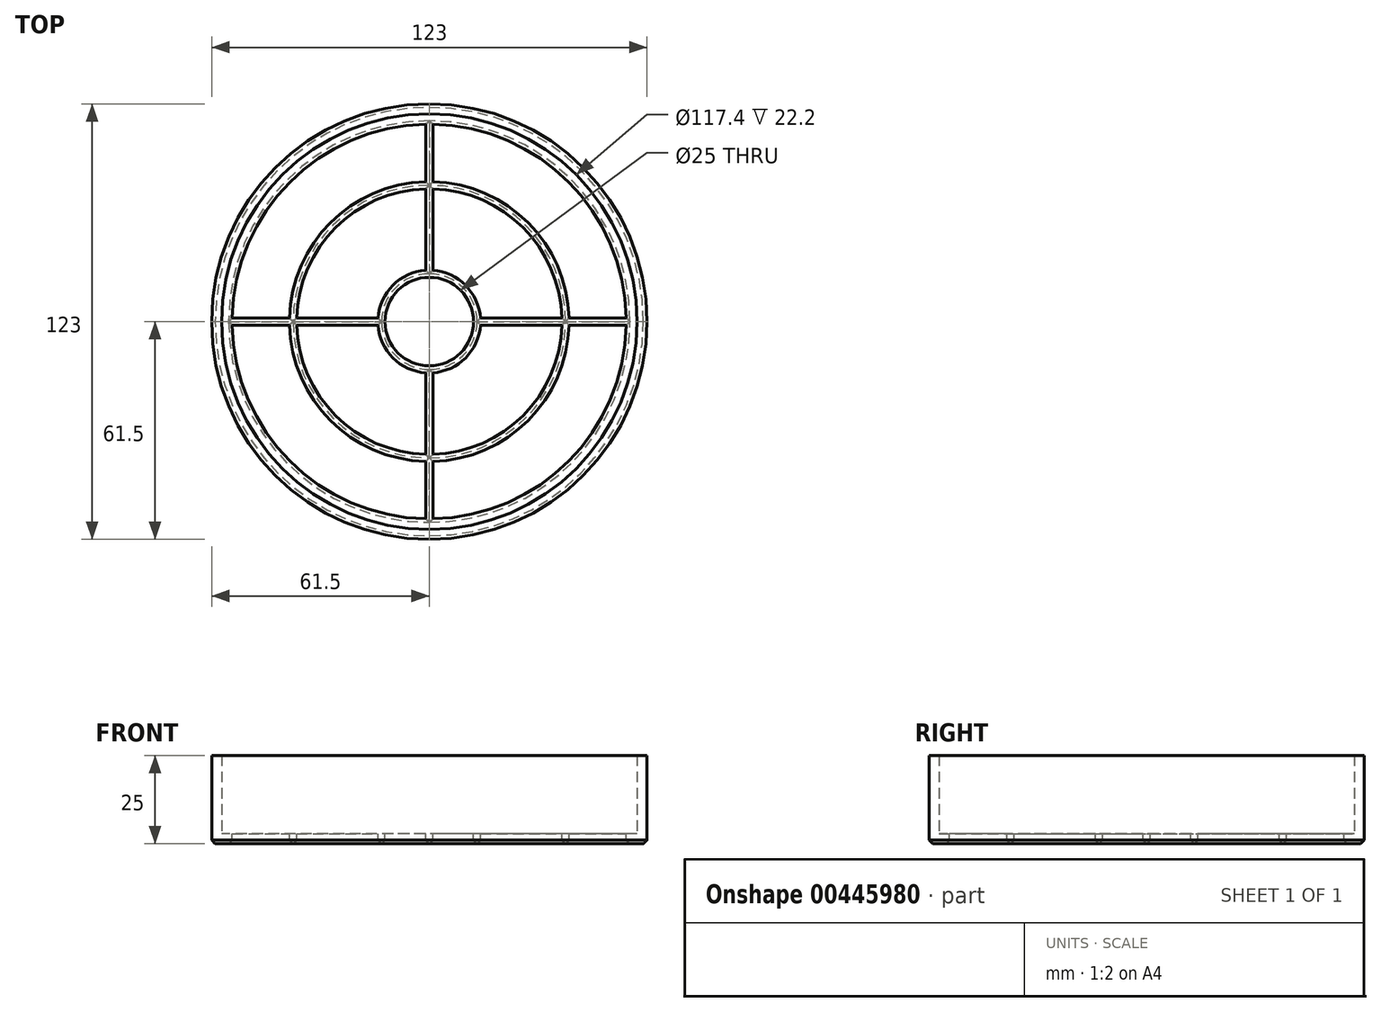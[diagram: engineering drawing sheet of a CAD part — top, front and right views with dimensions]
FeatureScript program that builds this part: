
annotation { "Feature Type Name" : "Feature", "Feature Type Description" : "" }
export const myFeature = defineFeature(function(context is Context, id is Id, definition is map)
    precondition{}
    {
        {
            var Q0;
            Q0=qCreatedBy(makeId("Top.planeOp"),FACE);
            var sketch = newSketch(context, id + "F0", { "sketchPlane" : qUnion([Q0])});
            skCircle(sketch, "E0", {"center": v(0, 0) * mm, "radius": 61.5 * mm});
            skSolve(sketch);
        }
        {
            var Q0;
            Q0=makeQuery(id+"F0.imprint","IMPRINT",FACE,{"disambiguationData":[TD([[makeQuery(id+"F0.imprint","IMPRINT",EDGE,{"derivedFrom":sQuery(id+"F0.wireOp",EDGE,"E0")}),1.0]])]});
            extrude(context, id + "F1", {"entities" : qUnion([Q0]), "depth" : 25 * mm});
        }
        {
            var Q0;
            Q0=makeQuery(id+"F1.opExtrude","CAP_FACE",FACE,{"disambiguationData":[OSD([sQuery(id+"F0.wireOp",EDGE,"E0")])],"isStart":false});
            shell(context, id + "F2", {"entities" : qUnion([Q0]), "thickness" : 2.8 * mm});
        }
        {
            var Q0;
            {var subQ0=sQuery(id+"F0.wireOp",EDGE,"E0");Q0=makeQuery(id+"F2.opShell","OFFSET_FACE",FACE,{"disambiguationData":[OSD([subQ0]),TDD([makeQuery(id+"F1.opExtrude","CAP_FACE",FACE,{"disambiguationData":[OSD([subQ0])],"isStart":true})])]});}
            var sketch = newSketch(context, id + "F3", { "sketchPlane" : qUnion([Q0])});
            skCircle(sketch, "E1", {"center": v(0, 0) * mm, "radius": 55.7 * mm});
            skCircle(sketch, "E2", {"center": v(0, 0) * mm, "radius": 39.5 * mm});
            skCircle(sketch, "E3", {"center": v(0, 0) * mm, "radius": 37.5 * mm});
            skCircle(sketch, "E4", {"center": v(0, 0) * mm, "radius": 14.5 * mm});
            skCircle(sketch, "E5", {"center": v(0, 0) * mm, "radius": 12.5 * mm});
            skLineSegment(sketch, "E6", {"start": v(-1, 55.7) * mm, "end": v(-1, -55.7) * mm});
            skLineSegment(sketch, "E7", {"start": v(1, 55.7) * mm, "end": v(1, -55.7) * mm});
            skPoint(sketch, "E8.center", {"position": v(-1, 0) * mm});
            skLineSegment(sketch, "E8.anchor1", {"start": v(-1, 0) * mm, "end": v(-1, -55.7) * mm, "construction": true});
            skLineSegment(sketch, "E9", {"start": v(-55.7, 1) * mm, "end": v(55.7, 1) * mm});
            skLineSegment(sketch, "E10", {"start": v(55.7, -1) * mm, "end": v(-55.7, -1) * mm});
            skSolve(sketch);
        }
        {
            var Q0;
            {var subQ0=sQuery(id+"F3.wireOp",EDGE,"E6");var subQ1=sQuery(id+"F3.wireOp",EDGE,"E3");var subQ2=makeQuery(id+"F3.imprint","INTERSECT",VERTEX,{"disambiguationData":[OD(0.0)],"derivedFrom":[subQ1,subQ0]});Q0=makeQuery(id+"F3.imprint","IMPRINT",FACE,{"disambiguationData":[TD([[makeQuery(id+"F3.imprint","IMPRINT",EDGE,{"disambiguationData":[TD([[subQ2,-1.0]])],"derivedFrom":subQ1}),1.0]])]});}
            var Q1;
            {var subQ0=sQuery(id+"F3.wireOp",EDGE,"E6");var subQ1=sQuery(id+"F3.wireOp",EDGE,"E1");var subQ2=makeQuery(id+"F3.imprint","INTERSECT",VERTEX,{"disambiguationData":[OD(0.0)],"derivedFrom":[subQ1,subQ0]});Q1=makeQuery(id+"F3.imprint","IMPRINT",FACE,{"disambiguationData":[TD([[makeQuery(id+"F3.imprint","IMPRINT",EDGE,{"disambiguationData":[TD([[subQ2,-1.0]])],"derivedFrom":subQ1}),1.0]])]});}
            var Q2;
            {var subQ0=sQuery(id+"F3.wireOp",EDGE,"E7");var subQ1=sQuery(id+"F3.wireOp",EDGE,"E1");var subQ2=makeQuery(id+"F3.imprint","INTERSECT",VERTEX,{"disambiguationData":[OD(0.0)],"derivedFrom":[subQ1,subQ0]});Q2=makeQuery(id+"F3.imprint","IMPRINT",FACE,{"disambiguationData":[TD([[makeQuery(id+"F3.imprint","IMPRINT",EDGE,{"disambiguationData":[TD([[subQ2,1.0]])],"derivedFrom":subQ1}),1.0]])]});}
            var Q3;
            {var subQ0=sQuery(id+"F3.wireOp",EDGE,"E7");var subQ1=sQuery(id+"F3.wireOp",EDGE,"E3");var subQ2=makeQuery(id+"F3.imprint","INTERSECT",VERTEX,{"disambiguationData":[OD(0.0)],"derivedFrom":[subQ1,subQ0]});Q3=makeQuery(id+"F3.imprint","IMPRINT",FACE,{"disambiguationData":[TD([[makeQuery(id+"F3.imprint","IMPRINT",EDGE,{"disambiguationData":[TD([[subQ2,1.0]])],"derivedFrom":subQ1}),1.0]])]});}
            var Q4;
            {var subQ0=sQuery(id+"F3.wireOp",EDGE,"E7");var subQ1=sQuery(id+"F3.wireOp",EDGE,"E1");var subQ2=makeQuery(id+"F3.imprint","INTERSECT",VERTEX,{"disambiguationData":[OD(1.0)],"derivedFrom":[subQ1,subQ0]});Q4=makeQuery(id+"F3.imprint","IMPRINT",FACE,{"disambiguationData":[TD([[makeQuery(id+"F3.imprint","IMPRINT",EDGE,{"disambiguationData":[TD([[subQ2,-1.0]])],"derivedFrom":subQ1}),1.0]])]});}
            var Q5;
            {var subQ0=sQuery(id+"F3.wireOp",EDGE,"E7");var subQ1=sQuery(id+"F3.wireOp",EDGE,"E3");var subQ2=makeQuery(id+"F3.imprint","INTERSECT",VERTEX,{"disambiguationData":[OD(1.0)],"derivedFrom":[subQ1,subQ0]});Q5=makeQuery(id+"F3.imprint","IMPRINT",FACE,{"disambiguationData":[TD([[makeQuery(id+"F3.imprint","IMPRINT",EDGE,{"disambiguationData":[TD([[subQ2,-1.0]])],"derivedFrom":subQ1}),1.0]])]});}
            var Q6;
            {var subQ0=sQuery(id+"F3.wireOp",EDGE,"E10");var subQ1=sQuery(id+"F3.wireOp",EDGE,"E3");var subQ2=makeQuery(id+"F3.imprint","INTERSECT",VERTEX,{"disambiguationData":[OD(0.0)],"derivedFrom":[subQ1,subQ0]});Q6=makeQuery(id+"F3.imprint","IMPRINT",FACE,{"disambiguationData":[TD([[makeQuery(id+"F3.imprint","IMPRINT",EDGE,{"disambiguationData":[TD([[subQ2,-1.0]])],"derivedFrom":subQ1}),1.0]])]});}
            var Q7;
            {var subQ0=sQuery(id+"F3.wireOp",EDGE,"E6");var subQ1=sQuery(id+"F3.wireOp",EDGE,"E1");var subQ2=makeQuery(id+"F3.imprint","INTERSECT",VERTEX,{"disambiguationData":[OD(1.0)],"derivedFrom":[subQ1,subQ0]});Q7=makeQuery(id+"F3.imprint","IMPRINT",FACE,{"disambiguationData":[TD([[makeQuery(id+"F3.imprint","IMPRINT",EDGE,{"disambiguationData":[TD([[subQ2,1.0]])],"derivedFrom":subQ1}),1.0]])]});}
            var Q8;
            {var subQ0=sQuery(id+"F3.wireOp",EDGE,"E10");var subQ1=sQuery(id+"F3.wireOp",EDGE,"E5");var subQ2=makeQuery(id+"F3.imprint","INTERSECT",VERTEX,{"disambiguationData":[OD(0.0)],"derivedFrom":[subQ1,subQ0]});Q8=makeQuery(id+"F3.imprint","IMPRINT",FACE,{"disambiguationData":[TD([[makeQuery(id+"F3.imprint","IMPRINT",EDGE,{"disambiguationData":[TD([[subQ2,-1.0]])],"derivedFrom":subQ1}),1.0]])]});}
            var Q9;
            {var subQ0=sQuery(id+"F3.wireOp",EDGE,"E9");var subQ1=sQuery(id+"F3.wireOp",EDGE,"E5");var subQ2=makeQuery(id+"F3.imprint","INTERSECT",VERTEX,{"disambiguationData":[OD(1.0)],"derivedFrom":[subQ1,subQ0]});Q9=makeQuery(id+"F3.imprint","IMPRINT",FACE,{"disambiguationData":[TD([[makeQuery(id+"F3.imprint","IMPRINT",EDGE,{"disambiguationData":[TD([[subQ2,-1.0]])],"derivedFrom":subQ1}),1.0]])]});}
            var Q10;
            {var subQ0=sQuery(id+"F3.wireOp",EDGE,"E6");var subQ1=sQuery(id+"F3.wireOp",EDGE,"E5");var subQ2=makeQuery(id+"F3.imprint","INTERSECT",VERTEX,{"disambiguationData":[OD(0.0)],"derivedFrom":[subQ1,subQ0]});Q10=makeQuery(id+"F3.imprint","IMPRINT",FACE,{"disambiguationData":[TD([[makeQuery(id+"F3.imprint","IMPRINT",EDGE,{"disambiguationData":[TD([[subQ2,-1.0]])],"derivedFrom":subQ1}),1.0]])]});}
            var Q11;
            {var subQ0=sQuery(id+"F3.wireOp",EDGE,"E7");var subQ1=sQuery(id+"F3.wireOp",EDGE,"E5");var subQ2=makeQuery(id+"F3.imprint","INTERSECT",VERTEX,{"disambiguationData":[OD(0.0)],"derivedFrom":[subQ1,subQ0]});Q11=makeQuery(id+"F3.imprint","IMPRINT",FACE,{"disambiguationData":[TD([[makeQuery(id+"F3.imprint","IMPRINT",EDGE,{"disambiguationData":[TD([[subQ2,-1.0]])],"derivedFrom":subQ1}),1.0]])]});}
            var Q12;
            {var subQ0=sQuery(id+"F3.wireOp",EDGE,"E7");var subQ1=sQuery(id+"F3.wireOp",EDGE,"E5");var subQ2=makeQuery(id+"F3.imprint","INTERSECT",VERTEX,{"disambiguationData":[OD(0.0)],"derivedFrom":[subQ1,subQ0]});Q12=makeQuery(id+"F3.imprint","IMPRINT",FACE,{"disambiguationData":[TD([[makeQuery(id+"F3.imprint","IMPRINT",EDGE,{"disambiguationData":[TD([[subQ2,1.0]])],"derivedFrom":subQ1}),1.0]])]});}
            var Q13;
            {var subQ0=sQuery(id+"F3.wireOp",EDGE,"E9");var subQ1=sQuery(id+"F3.wireOp",EDGE,"E5");var subQ2=makeQuery(id+"F3.imprint","INTERSECT",VERTEX,{"disambiguationData":[OD(0.0)],"derivedFrom":[subQ1,subQ0]});Q13=makeQuery(id+"F3.imprint","IMPRINT",FACE,{"disambiguationData":[TD([[makeQuery(id+"F3.imprint","IMPRINT",EDGE,{"disambiguationData":[TD([[subQ2,1.0]])],"derivedFrom":subQ1}),1.0]])]});}
            var Q14;
            {var subQ0=sQuery(id+"F3.wireOp",EDGE,"E7");var subQ1=sQuery(id+"F3.wireOp",EDGE,"E5");var subQ2=makeQuery(id+"F3.imprint","INTERSECT",VERTEX,{"disambiguationData":[OD(1.0)],"derivedFrom":[subQ1,subQ0]});Q14=makeQuery(id+"F3.imprint","IMPRINT",FACE,{"disambiguationData":[TD([[makeQuery(id+"F3.imprint","IMPRINT",EDGE,{"disambiguationData":[TD([[subQ2,-1.0]])],"derivedFrom":subQ1}),1.0]])]});}
            var Q15;
            {var subQ0=sQuery(id+"F3.wireOp",EDGE,"E6");var subQ1=sQuery(id+"F3.wireOp",EDGE,"E5");var subQ2=makeQuery(id+"F3.imprint","INTERSECT",VERTEX,{"disambiguationData":[OD(1.0)],"derivedFrom":[subQ1,subQ0]});Q15=makeQuery(id+"F3.imprint","IMPRINT",FACE,{"disambiguationData":[TD([[makeQuery(id+"F3.imprint","IMPRINT",EDGE,{"disambiguationData":[TD([[subQ2,-1.0]])],"derivedFrom":subQ1}),1.0]])]});}
            var Q16;
            {var subQ0=sQuery(id+"F3.wireOp",EDGE,"E9");var subQ1=sQuery(id+"F3.wireOp",EDGE,"E6");var subQ2=makeQuery(id+"F3.imprint","INTERSECT",VERTEX,{"derivedFrom":[subQ1,subQ0]});Q16=makeQuery(id+"F3.imprint","IMPRINT",FACE,{"disambiguationData":[TD([[makeQuery(id+"F3.imprint","IMPRINT",EDGE,{"disambiguationData":[TD([[subQ2,-1.0]])],"derivedFrom":subQ1}),1.0]])]});}
            extrude(context, id + "F4", {"entities" : qUnion([Q0, Q1, Q2, Q3, Q4, Q5, Q6, Q7, Q8, Q9, Q10, Q11, Q12, Q13, Q14, Q15, Q16]), "operationType" : NewBodyOperationType.REMOVE, "endBound" : BoundingType.THROUGH_ALL, "oppositeDirection" : true, "depth" : 25 * mm});
        }
        {
            var Q0;
            {var subQ0=sQuery(id+"F0.wireOp",EDGE,"E0");Q0=makeQuery(id+"F2.opShell","OFFSET_FACE",FACE,{"disambiguationData":[OSD([subQ0]),TDD([makeQuery(id+"F1.opExtrude","CAP_FACE",FACE,{"disambiguationData":[OSD([subQ0])],"isStart":true})])]});}
            var sketch = newSketch(context, id + "F5", { "sketchPlane" : qUnion([Q0])});
            skCircle(sketch, "E11", {"center": v(0, 0) * mm, "radius": 14.5 * mm});
            skCircle(sketch, "E12", {"center": v(0, 0) * mm, "radius": 37.5 * mm});
            skCircle(sketch, "E13", {"center": v(0, 0) * mm, "radius": 39.5 * mm});
            skCircle(sketch, "E14", {"center": v(0, 0) * mm, "radius": 55.7 * mm});
            skSolve(sketch);
        }
        {
            var Q0;
            Q0=makeQuery(id+"F1.opExtrude","CAP_FACE",FACE,{"disambiguationData":[OSD([sQuery(id+"F0.wireOp",EDGE,"E0")])],"isStart":true});
            chamfer(context, id + "F6", {"entities" : qUnion([Q0]), "width" : 1 * mm, "tangentPropagation" : true});
        }
    });
